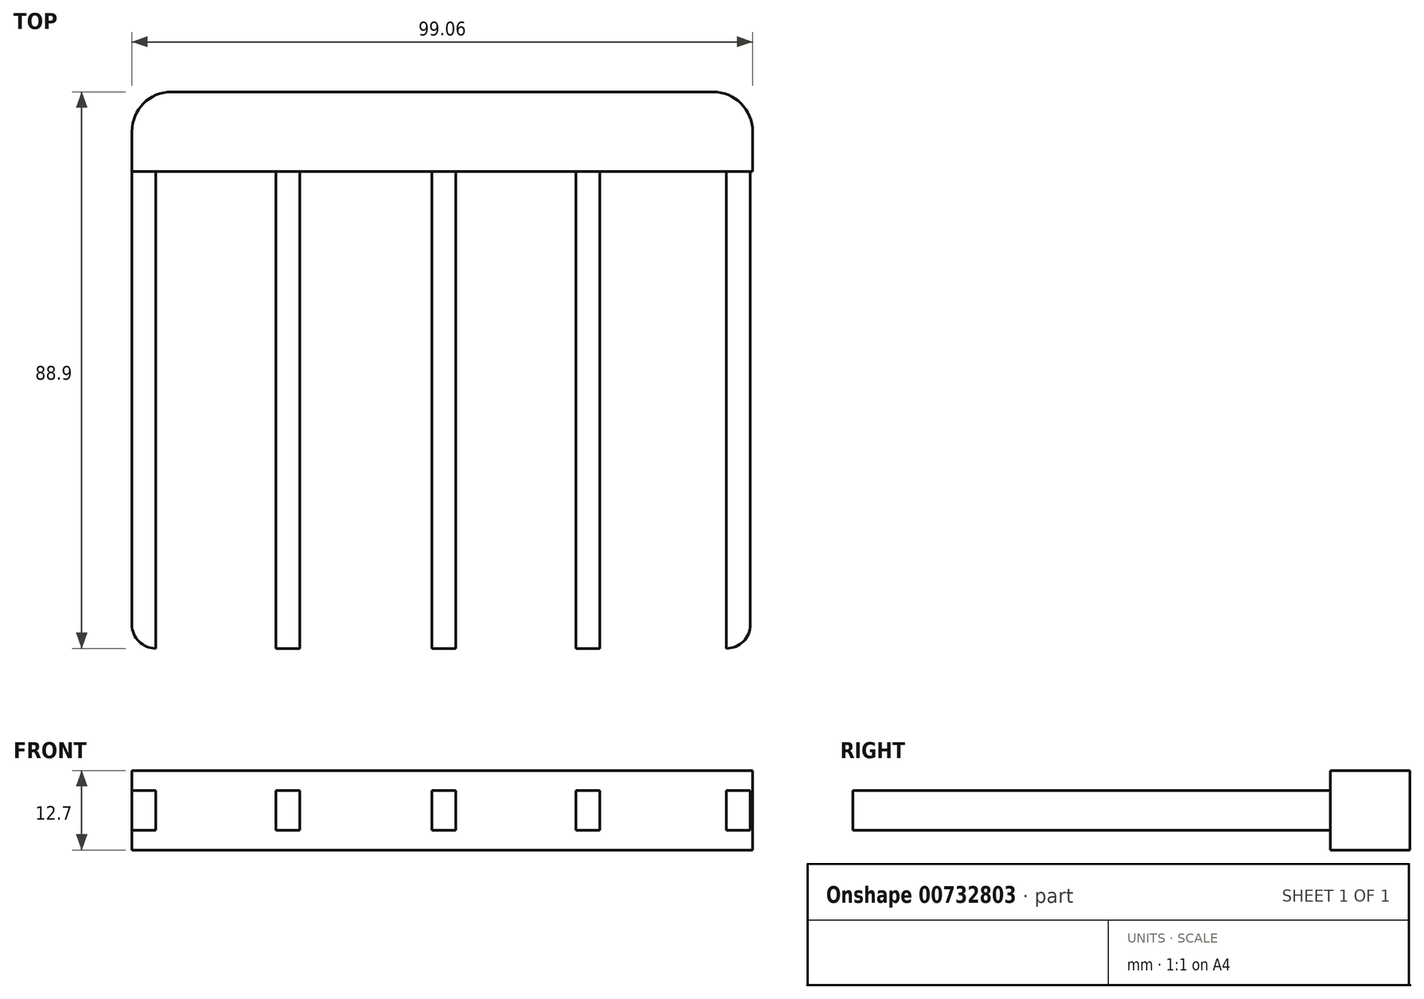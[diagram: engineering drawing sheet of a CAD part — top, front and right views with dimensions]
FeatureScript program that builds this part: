
annotation { "Feature Type Name" : "Feature", "Feature Type Description" : "" }
export const myFeature = defineFeature(function(context is Context, id is Id, definition is map)
    precondition{}
    {
        {
            var Q0;
            Q0=qCreatedBy(makeId("Top.planeOp"),FACE);
            var sketch = newSketch(context, id + "F0", { "sketchPlane" : qUnion([Q0])});
            skLineSegment(sketch, "E0.bottom", {"start": v(-49.2, 21.8) * mm, "end": v(49.85, 21.8) * mm});
            skLineSegment(sketch, "E0.top", {"start": v(-42.86, 34.5) * mm, "end": v(43.5, 34.5) * mm});
            skLineSegment(sketch, "E0.left", {"start": v(-49.2, 21.8) * mm, "end": v(-49.2, 28.15) * mm});
            skLineSegment(sketch, "E0.right", {"start": v(49.85, 21.8) * mm, "end": v(49.85, 28.15) * mm});
            skLineSegment(sketch, "E1.top", {"start": v(-45.4, -54.4) * mm, "end": v(-45.4, -54.4) * mm});
            skLineSegment(sketch, "E1.left", {"start": v(-49.2, 21.8) * mm, "end": v(-49.2, -50.6) * mm});
            skLineSegment(sketch, "E1.right", {"start": v(-45.4, 21.8) * mm, "end": v(-45.4, -54.4) * mm});
            skPoint(sketch, "E2.visualSharp", {"position": v(-49.2, 34.5) * mm});
            skArc(sketch, "E2.filletArc", {"start": v(-42.86, 34.5) * mm, "mid": v(-47.35, 32.64) * mm, "end": v(-49.2, 28.15) * mm});
            skPoint(sketch, "E3.visualSharp", {"position": v(49.85, 34.5) * mm});
            skArc(sketch, "E3.filletArc", {"start": v(49.85, 28.15) * mm, "mid": v(48, 32.64) * mm, "end": v(43.5, 34.5) * mm});
            skLineSegment(sketch, "E4.top", {"start": v(-26.26, -54.4) * mm, "end": v(-22.45, -54.4) * mm});
            skLineSegment(sketch, "E4.left", {"start": v(-26.26, 21.8) * mm, "end": v(-26.26, -54.4) * mm});
            skLineSegment(sketch, "E4.right", {"start": v(-22.45, 21.8) * mm, "end": v(-22.45, -54.4) * mm});
            skLineSegment(sketch, "E5.top", {"start": v(45.67, -54.4) * mm, "end": v(45.67, -54.4) * mm});
            skLineSegment(sketch, "E5.left", {"start": v(45.67, 21.8) * mm, "end": v(45.67, -54.4) * mm});
            skLineSegment(sketch, "E5.right", {"start": v(49.48, 21.8) * mm, "end": v(49.48, -50.6) * mm});
            skPoint(sketch, "E6.visualSharp", {"position": v(49.48, -54.4) * mm});
            skArc(sketch, "E6.filletArc", {"start": v(45.67, -54.4) * mm, "mid": v(48.37, -53.29) * mm, "end": v(49.48, -50.6) * mm});
            skPoint(sketch, "E7.visualSharp", {"position": v(-49.2, -54.4) * mm});
            skArc(sketch, "E7.filletArc", {"start": v(-49.2, -50.6) * mm, "mid": v(-48.1, -53.29) * mm, "end": v(-45.4, -54.4) * mm});
            skLineSegment(sketch, "E8.top", {"start": v(-1.32, -54.4) * mm, "end": v(2.49, -54.4) * mm});
            skLineSegment(sketch, "E8.left", {"start": v(-1.32, 21.8) * mm, "end": v(-1.32, -54.4) * mm});
            skLineSegment(sketch, "E8.right", {"start": v(2.49, 21.8) * mm, "end": v(2.49, -54.4) * mm});
            skLineSegment(sketch, "E9.top", {"start": v(21.66, -54.4) * mm, "end": v(25.47, -54.4) * mm});
            skLineSegment(sketch, "E9.left", {"start": v(21.66, 21.8) * mm, "end": v(21.66, -54.4) * mm});
            skLineSegment(sketch, "E9.right", {"start": v(25.47, 21.8) * mm, "end": v(25.47, -54.4) * mm});
            skSolve(sketch);
        }
        {
            var Q0;
            Q0=makeQuery(id+"F0.imprint","IMPRINT",FACE,{"disambiguationData":[TD([[makeQuery(id+"F0.imprint","IMPRINT",EDGE,{"derivedFrom":sQuery(id+"F0.wireOp",EDGE,"E0.top")}),-1.0]])]});
            extrude(context, id + "F1", {"entities" : qUnion([Q0]), "endBound" : BoundingType.SYMMETRIC, "depth" : 12.7 * mm, "offsetDistance" : 25.4 * mm});
        }
        {
            var Q0;
            Q0 = qSketchRegion(id + "F0", true);
            extrude(context, id + "F2", {"entities" : qUnion([Q0]), "operationType" : NewBodyOperationType.ADD, "endBound" : BoundingType.SYMMETRIC, "depth" : 6.35 * mm, "offsetDistance" : 25.4 * mm});
        }
    });
